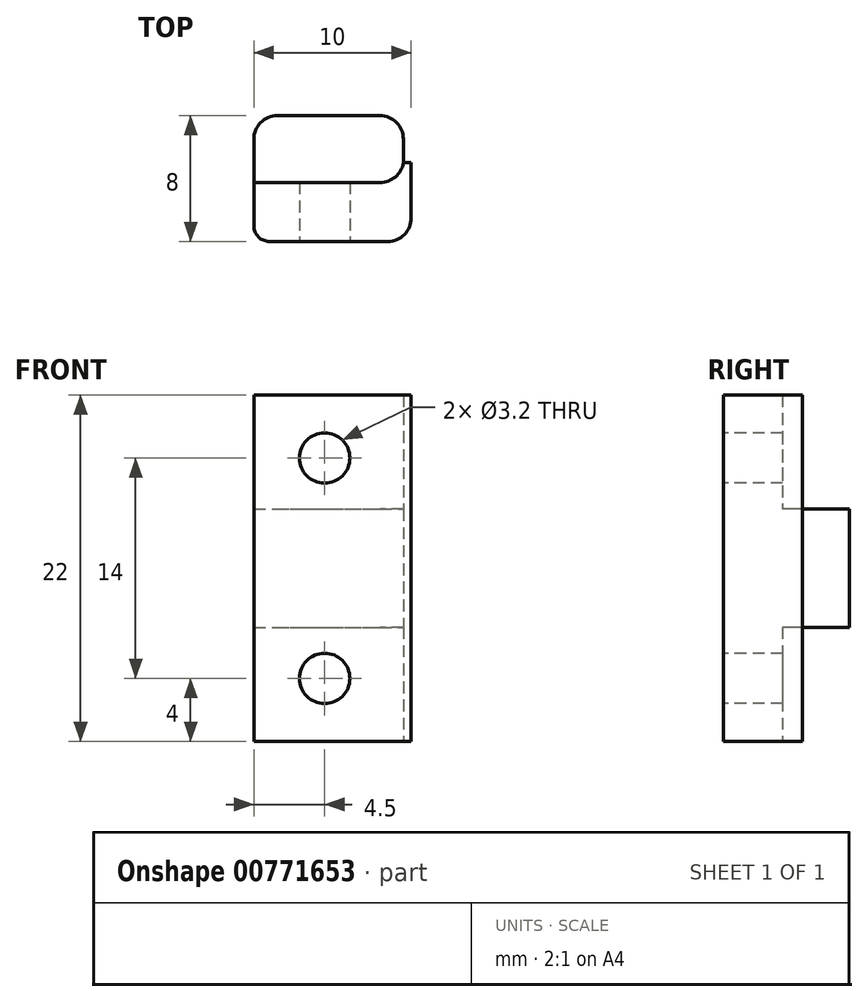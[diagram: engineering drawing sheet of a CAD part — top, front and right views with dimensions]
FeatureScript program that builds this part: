
annotation { "Feature Type Name" : "Feature", "Feature Type Description" : "" }
export const myFeature = defineFeature(function(context is Context, id is Id, definition is map)
    precondition{}
    {
        {
            var Q0;
            Q0=qCreatedBy(makeId("Front.planeOp"),FACE);
            var sketch = newSketch(context, id + "F0", { "sketchPlane" : qUnion([Q0])});
            skLineSegment(sketch, "E0.bottom", {"start": v(-6, 11) * mm, "end": v(4, 11) * mm});
            skLineSegment(sketch, "E0.top", {"start": v(-6, -11) * mm, "end": v(4, -11) * mm});
            skLineSegment(sketch, "E0.left", {"start": v(-6, 11) * mm, "end": v(-6, -11) * mm});
            skLineSegment(sketch, "E0.right", {"start": v(4, 11) * mm, "end": v(4, -11) * mm});
            skSolve(sketch);
        }
        {
            var Q0;
            Q0 = qSketchRegion(id + "F0", true);
            extrude(context, id + "F1", {"entities" : qUnion([Q0]), "depth" : 5 * mm, "offsetDistance" : 25 * mm});
        }
        {
            var Q0;
            Q0=makeQuery(id+"F1.opExtrude","SWEPT_FACE",FACE,{"disambiguationData":[OSD([sQuery(id+"F0.wireOp",EDGE,"E0.top")])]});
            var sketch = newSketch(context, id + "F2", { "sketchPlane" : qUnion([Q0])});
            skLineSegment(sketch, "E1.bottom", {"start": v(-6, 1.25) * mm, "end": v(3.5, 1.25) * mm});
            skLineSegment(sketch, "E1.top", {"start": v(-6, 0) * mm, "end": v(3.5, 0) * mm});
            skLineSegment(sketch, "E1.left", {"start": v(-6, 1.25) * mm, "end": v(-6, 0) * mm});
            skLineSegment(sketch, "E1.right", {"start": v(3.5, 1.25) * mm, "end": v(3.5, 0) * mm});
            skSolve(sketch);
        }
        {
            var Q0;
            Q0 = qSketchRegion(id + "F2", true);
            extrude(context, id + "F3", {"entities" : qUnion([Q0]), "operationType" : NewBodyOperationType.REMOVE, "endBound" : BoundingType.UP_TO_NEXT, "oppositeDirection" : true, "depth" : 25 * mm, "offsetDistance" : 25 * mm});
        }
        {
            var Q0;
            Q0=makeQuery(id+"F1.opExtrude","CAP_EDGE",EDGE,{"disambiguationData":[OSD([sQuery(id+"F0.wireOp",EDGE,"E0.right")])],"isStart":false});
            fillet(context, id + "F4", {"entities" : qUnion([Q0]), "radius" : 1.5 * mm, "tangentPropagation" : true, "allowEdgeOverflow" : false});
        }
        {
            var Q0;
            Q0=makeQuery(id+"F1.opExtrude","CAP_FACE",FACE,{"disambiguationData":[OSD([sQuery(id+"F0.wireOp",EDGE,"E0.bottom"),sQuery(id+"F0.wireOp",EDGE,"E0.top"),sQuery(id+"F0.wireOp",EDGE,"E0.left"),sQuery(id+"F0.wireOp",EDGE,"E0.right")])],"isStart":false});
            var sketch = newSketch(context, id + "F5", { "sketchPlane" : qUnion([Q0])});
            skCircle(sketch, "E2", {"center": v(-1.5, 7) * mm, "radius": 1.6 * mm});
            skCircle(sketch, "E3", {"center": v(-1.5, -7) * mm, "radius": 1.6 * mm});
            skSolve(sketch);
        }
        {
            var Q0;
            Q0 = qSketchRegion(id + "F5", true);
            extrude(context, id + "F6", {"entities" : qUnion([Q0]), "operationType" : NewBodyOperationType.REMOVE, "endBound" : BoundingType.UP_TO_NEXT, "oppositeDirection" : true, "depth" : 25 * mm, "offsetDistance" : 25 * mm});
        }
        {
            var Q0;
            Q0=makeQuery(id+"F3.boolean.opBoolean","COPY",FACE,{"derivedFrom":makeQuery(id+"F3.opExtrude","SWEPT_FACE",FACE,{"disambiguationData":[OSD([sQuery(id+"F2.wireOp",EDGE,"E1.bottom")])]})});
            var sketch = newSketch(context, id + "F7", { "sketchPlane" : qUnion([Q0])});
            skLineSegment(sketch, "E4.bottom", {"start": v(6, 3.75) * mm, "end": v(-3.5, 3.75) * mm});
            skLineSegment(sketch, "E4.top", {"start": v(6, -3.75) * mm, "end": v(-3.5, -3.75) * mm});
            skLineSegment(sketch, "E4.left", {"start": v(6, 3.75) * mm, "end": v(6, -3.75) * mm});
            skLineSegment(sketch, "E4.right", {"start": v(-3.5, 3.75) * mm, "end": v(-3.5, -3.75) * mm});
            skSolve(sketch);
        }
        {
            var Q0;
            Q0 = qSketchRegion(id + "F7", true);
            extrude(context, id + "F8", {"entities" : qUnion([Q0]), "operationType" : NewBodyOperationType.ADD, "depth" : 4.25 * mm, "offsetDistance" : 25 * mm});
        }
        {
            var Q0;
            {var subQ0=sQuery(id+"F2.wireOp",EDGE,"E1.bottom");var subQ1=sQuery(id+"F2.wireOp",EDGE,"E1.right");Q0=makeQuery(id+"F8.boolean.opBoolean","SPLIT",EDGE,{"disambiguationData":[TD([makeQuery(id+"F1.opExtrude","SWEPT_FACE",FACE,{"disambiguationData":[OSD([sQuery(id+"F0.wireOp",EDGE,"E0.top")])]})])],"derivedFrom":makeQuery(id+"F3.boolean.opBoolean","COPY",EDGE,{"derivedFrom":makeQuery(id+"F3.opExtrude","SWEPT_EDGE",EDGE,{"disambiguationData":[OSD([subQ0,subQ1])]})})});}
            var Q1;
            {var subQ0=sQuery(id+"F2.wireOp",EDGE,"E1.right");var subQ1=sQuery(id+"F2.wireOp",EDGE,"E1.bottom");Q1=makeQuery(id+"F8.boolean.opBoolean","SPLIT",EDGE,{"disambiguationData":[TD([makeQuery(id+"F1.opExtrude","SWEPT_FACE",FACE,{"disambiguationData":[OSD([sQuery(id+"F0.wireOp",EDGE,"E0.bottom")])]})])],"derivedFrom":makeQuery(id+"F3.boolean.opBoolean","COPY",EDGE,{"derivedFrom":makeQuery(id+"F3.opExtrude","SWEPT_EDGE",EDGE,{"disambiguationData":[OSD([subQ1,subQ0])]})})});}
            var Q2;
            Q2=makeQuery(id+"F8.opExtrude","CAP_EDGE",EDGE,{"disambiguationData":[OSD([sQuery(id+"F7.wireOp",EDGE,"E4.right")])],"isStart":false});
            var Q3;
            Q3=makeQuery(id+"F8.opExtrude","CAP_EDGE",EDGE,{"disambiguationData":[OSD([sQuery(id+"F7.wireOp",EDGE,"E4.left")])],"isStart":false});
            fillet(context, id + "F9", {"entities" : qUnion([Q0, Q1, Q2, Q3]), "radius" : 1.5 * mm, "tangentPropagation" : true, "allowEdgeOverflow" : false});
        }
        {
            var Q0;
            Q0=makeQuery(id+"F1.opExtrude","CAP_EDGE",EDGE,{"disambiguationData":[OSD([sQuery(id+"F0.wireOp",EDGE,"E0.left")])],"isStart":false});
            fillet(context, id + "F10", {"entities" : qUnion([Q0]), "radius" : 1 * mm, "tangentPropagation" : true, "allowEdgeOverflow" : false});
        }
    });
